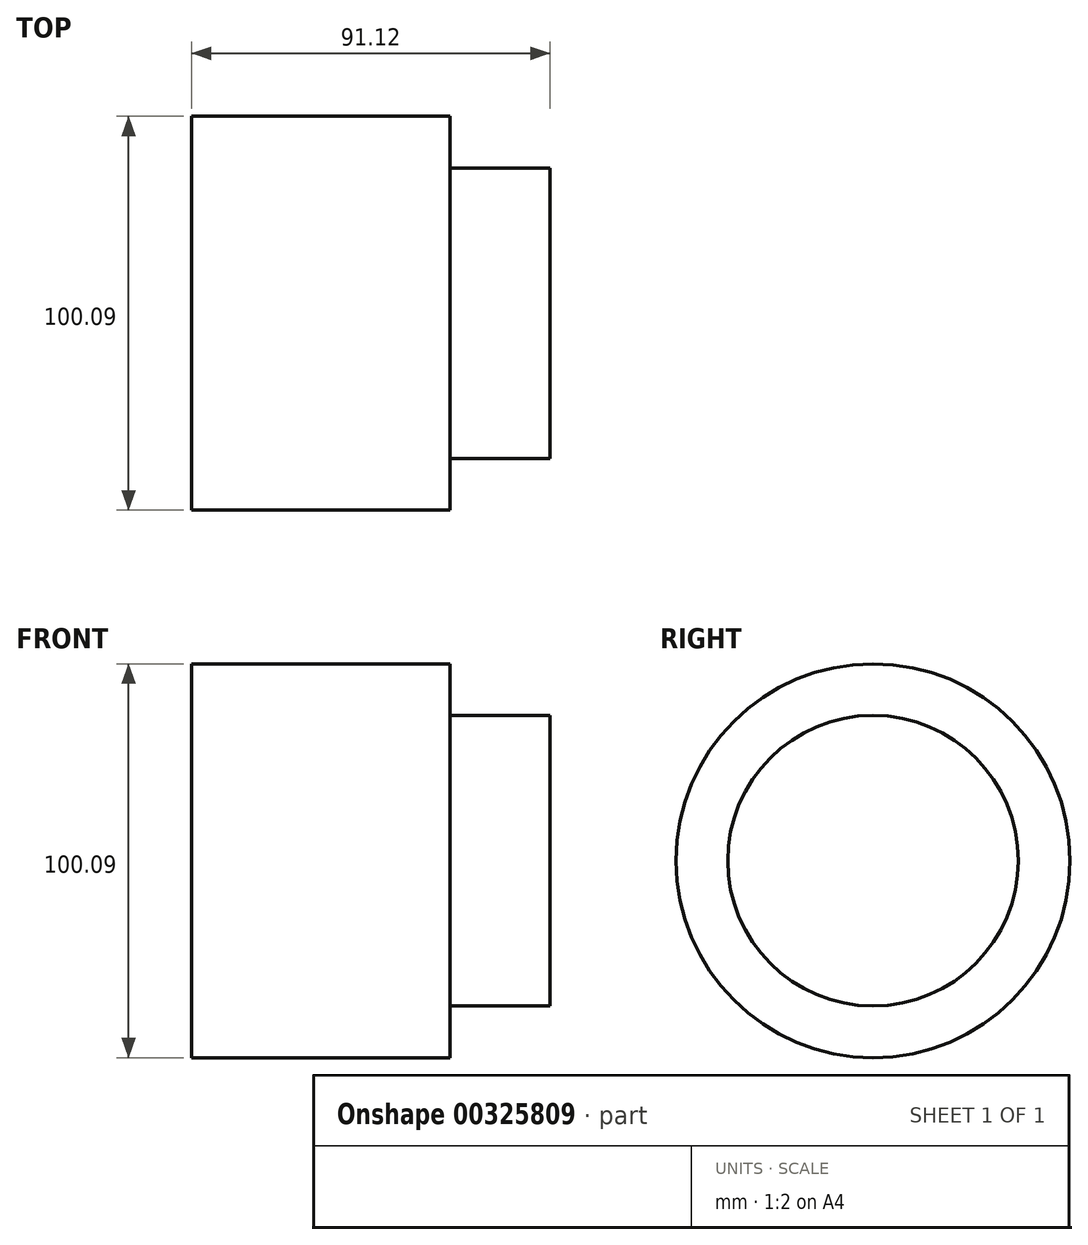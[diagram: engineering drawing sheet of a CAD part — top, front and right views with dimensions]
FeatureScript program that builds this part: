
annotation { "Feature Type Name" : "Feature", "Feature Type Description" : "" }
export const myFeature = defineFeature(function(context is Context, id is Id, definition is map)
    precondition{}
    {
        {
            var Q0;
            Q0=qCreatedBy(makeId("Right.planeOp"),FACE);
            var sketch = newSketch(context, id + "F0", { "sketchPlane" : qUnion([Q0])});
            skCircle(sketch, "E0", {"center": v(19.09, -39.97) * mm, "radius": 50.05 * mm});
            skSolve(sketch);
        }
        {
            var Q0;
            Q0 = qSketchRegion(id + "F0", true);
            extrude(context, id + "F1", {"entities" : qUnion([Q0]), "oppositeDirection" : true, "depth" : 65.72 * mm});
        }
        {
            var Q0;
            Q0=makeQuery(id+"F1.opExtrude","CAP_FACE",FACE,{"disambiguationData":[OSD([sQuery(id+"F0.wireOp",EDGE,"E0")])],"isStart":true});
            var sketch = newSketch(context, id + "F2", { "sketchPlane" : qUnion([Q0])});
            skCircle(sketch, "E1", {"center": v(19.09, -39.97) * mm, "radius": 36.91 * mm});
            skSolve(sketch);
        }
        {
            var Q0;
            Q0=makeQuery(id+"F2.imprint","IMPRINT",FACE,{"disambiguationData":[TD([[makeQuery(id+"F2.imprint","IMPRINT",EDGE,{"derivedFrom":sQuery(id+"F2.wireOp",EDGE,"E1")}),1.0]])]});
            var Q1;
            Q1=makeQuery(id+"F1.opExtrude","CAP_FACE",FACE,{"disambiguationData":[OSD([sQuery(id+"F0.wireOp",EDGE,"E0")])],"isStart":false});
            extrude(context, id + "F3", {"entities" : qUnion([Q0, Q1]), "operationType" : NewBodyOperationType.ADD, "depth" : 25.4 * mm});
        }
    });
